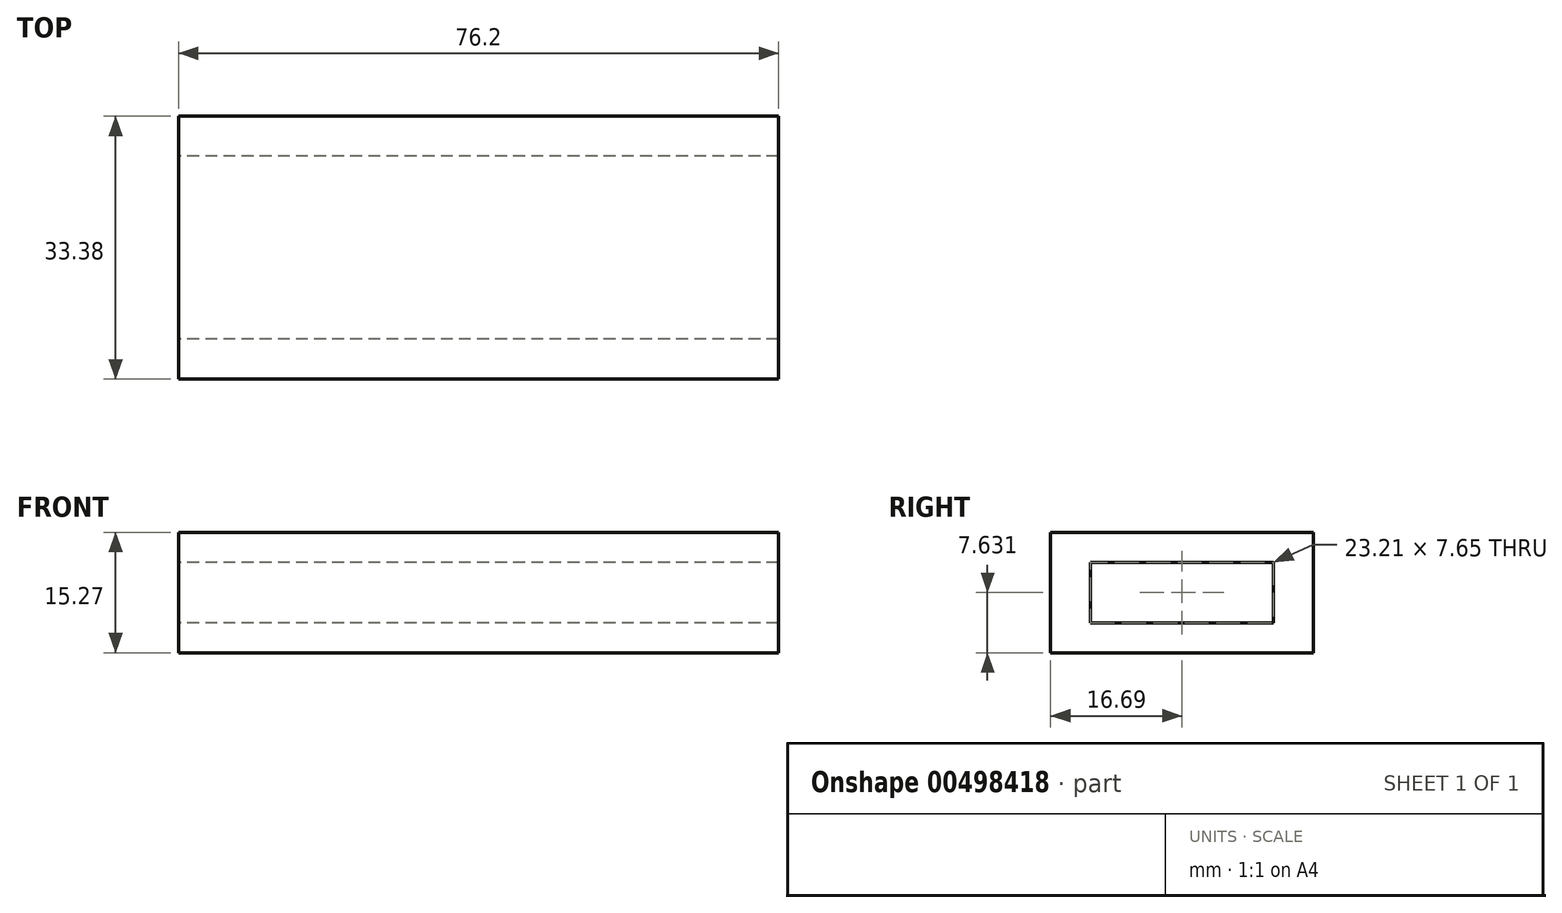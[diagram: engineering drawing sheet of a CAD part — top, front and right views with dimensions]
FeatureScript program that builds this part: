
annotation { "Feature Type Name" : "Feature", "Feature Type Description" : "" }
export const myFeature = defineFeature(function(context is Context, id is Id, definition is map)
    precondition{}
    {
        {
            var Q0;
            Q0=qCreatedBy(makeId("Top.planeOp"),FACE);
            var sketch = newSketch(context, id + "F0", { "sketchPlane" : qUnion([Q0])});
            skLineSegment(sketch, "E0.bottom", {"start": v(38.1, 16.69) * mm, "end": v(-38.1, 16.69) * mm});
            skLineSegment(sketch, "E0.top", {"start": v(38.1, -16.69) * mm, "end": v(-38.1, -16.69) * mm});
            skLineSegment(sketch, "E0.left", {"start": v(38.1, 16.69) * mm, "end": v(38.1, -16.69) * mm});
            skLineSegment(sketch, "E0.right", {"start": v(-38.1, 16.69) * mm, "end": v(-38.1, -16.69) * mm});
            skPoint(sketch, "E0.middle", {"position": v(0, 0) * mm});
            skSolve(sketch);
        }
        {
            var Q0;
            Q0=makeQuery(id+"F0.imprint","IMPRINT",FACE,{"disambiguationData":[TD([[makeQuery(id+"F0.imprint","IMPRINT",EDGE,{"derivedFrom":sQuery(id+"F0.wireOp",EDGE,"E0.bottom")}),1.0]])]});
            extrude(context, id + "F1", {"entities" : qUnion([Q0]), "depth" : 15.27 * mm});
        }
        {
            var Q0;
            Q0=makeQuery(id+"F1.opExtrude","SWEPT_FACE",FACE,{"disambiguationData":[OSD([sQuery(id+"F0.wireOp",EDGE,"E0.right")])]});
            var sketch = newSketch(context, id + "F2", { "sketchPlane" : qUnion([Q0])});
            skLineSegment(sketch, "E1.bottom", {"start": v(-11.6, 11.46) * mm, "end": v(11.6, 11.46) * mm});
            skLineSegment(sketch, "E1.top", {"start": v(-11.6, 3.8) * mm, "end": v(11.6, 3.8) * mm});
            skLineSegment(sketch, "E1.left", {"start": v(-11.6, 11.46) * mm, "end": v(-11.6, 3.8) * mm});
            skLineSegment(sketch, "E1.right", {"start": v(11.6, 11.46) * mm, "end": v(11.6, 3.8) * mm});
            skPoint(sketch, "E1.middle", {"position": v(0, 7.63) * mm});
            skSolve(sketch);
        }
        {
            var Q0;
            Q0=makeQuery(id+"F2.imprint","IMPRINT",FACE,{"disambiguationData":[TD([[makeQuery(id+"F2.imprint","IMPRINT",EDGE,{"derivedFrom":sQuery(id+"F2.wireOp",EDGE,"E1.bottom")}),-1.0]])]});
            extrude(context, id + "F3", {"entities" : qUnion([Q0]), "operationType" : NewBodyOperationType.REMOVE, "oppositeDirection" : true, "depth" : 127 * mm});
        }
    });
